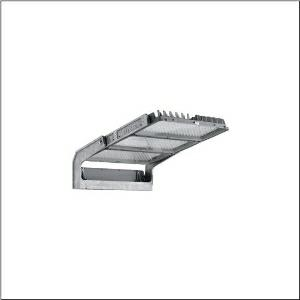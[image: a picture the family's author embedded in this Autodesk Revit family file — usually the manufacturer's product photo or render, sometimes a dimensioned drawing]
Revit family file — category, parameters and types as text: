
# Revit family: floodlight_fl_11_maxi_pro___rs07_5xa779124k02fb_0e28
name_source: partatom
category: Lighting Fixtures
units: mm (PartAtom-declared; Revit-internal decimal feet)

## family parameters
Cut with Voids When Loaded = No
Host = Face
Light Source = No
Part Type = Normal
Room Calculation Point = No
Round Connector Dimension = Use Diameter
Shared = No

## types (1)
- --- (1 x LED, 130880 lm, 1323.9 W, 5700K)
    Apparent Load = 1324 VA
    CIE Flux Codes = 80 93 99 100 99
    Color Rendering = 90
    Color Temperature = 5700K
    Default Elevation = 1800 mm
    Description = Floodlight FL 11  maxi  pro floodlight; light control with lens of PMMA; cover panel of toughened safety glass, transparent; light distribution: RS07, rotationally symmetric direct distribution, LEDcolour temperature: 5700K, rated luminous flux: 130.880lm, colour rendering: CRI > 90, light colour: 957; luminous efficacy: 99lm/W; brightness control: DALI 2; with terminal, 5-pole, max. 2.5mm², mains connection: 220..240V/380..400V AC, 50/60Hz, surge voltage resistance: line to ground: 10kV, service life up to 100,000h L90. Typical operating time: 1000h per year, ECG replaceable separately, LED unit replaceable without ESD environment, dustproof LED module, dimming range 10..100%; 1324W floodlight with 3x LED unit of diecast aluminium, coated grey; length: 1.003mm / width: 651mm / height: 338mm; mounting bracket, of diecast aluminium, uncoated, natural, protection rating (complete): IP66; insulation class (complete): insulation class I (protective earthing); certification: CE, ENEC, VDE; ball protection: ball impact resistant, only for outdoor installations in the designated locations, permissible operating ambient temperature: -45..+55°C, permissible storage temperature: -40..+85°Cpackaging unit: 1 piece

Light Distribution: RS07
    Height = 320 mm
    Lamp = 1 x LED
    Lamp Light Flux = 130880 lm
    Lamp Power = 1323.9 W
    Lamp count = 1
    Length = 1002 mm
    Luminous efficacy = 99 lm/W
    Manufacturer = Siteco
    ModVariant = No
    Model = 5XA779124K02FB
    Mounting Place = Ceiling
    Mounting Type = Surface mounted
    Number of Poles = 1
    OnlyDefault = Yes
    Power Factor = 1
    Product Name = Floodlight FL 11 maxi pro | RS07
    Product group = floodlight | ceiling mounted
    ProductGroupID = 301
    Protection Class = Protection class I
    Protection Degree = IP 66
    RLX_Detail_Level = 1
    RLX_Emergency_Light_Flux = 0 lm
    RLX_Emergency_Type = 0
    RLX_Emergency_Type_DB = No
    RlxData = <blob elided: 40197 chars, md5=52805208>
    Socket = socket
    Standby Power = 0 W
    System Light Flux = 130880 lm
    System Power = 1324 W
    Type Comments = factory setting: luminous flux: 100 % | dim-lin: 254 | 900 mA
    Type Image = l_1356210.jpg
    URL = http://relux.com
    VarID = @adj_023458
    Voltage = 0 V
    Weight = 0.00 kg
    Width = 655 mm

## geometry (parser evidence)
native form markers: Blend x4, Sweep x12
no freeform markers — native parametric forms only
